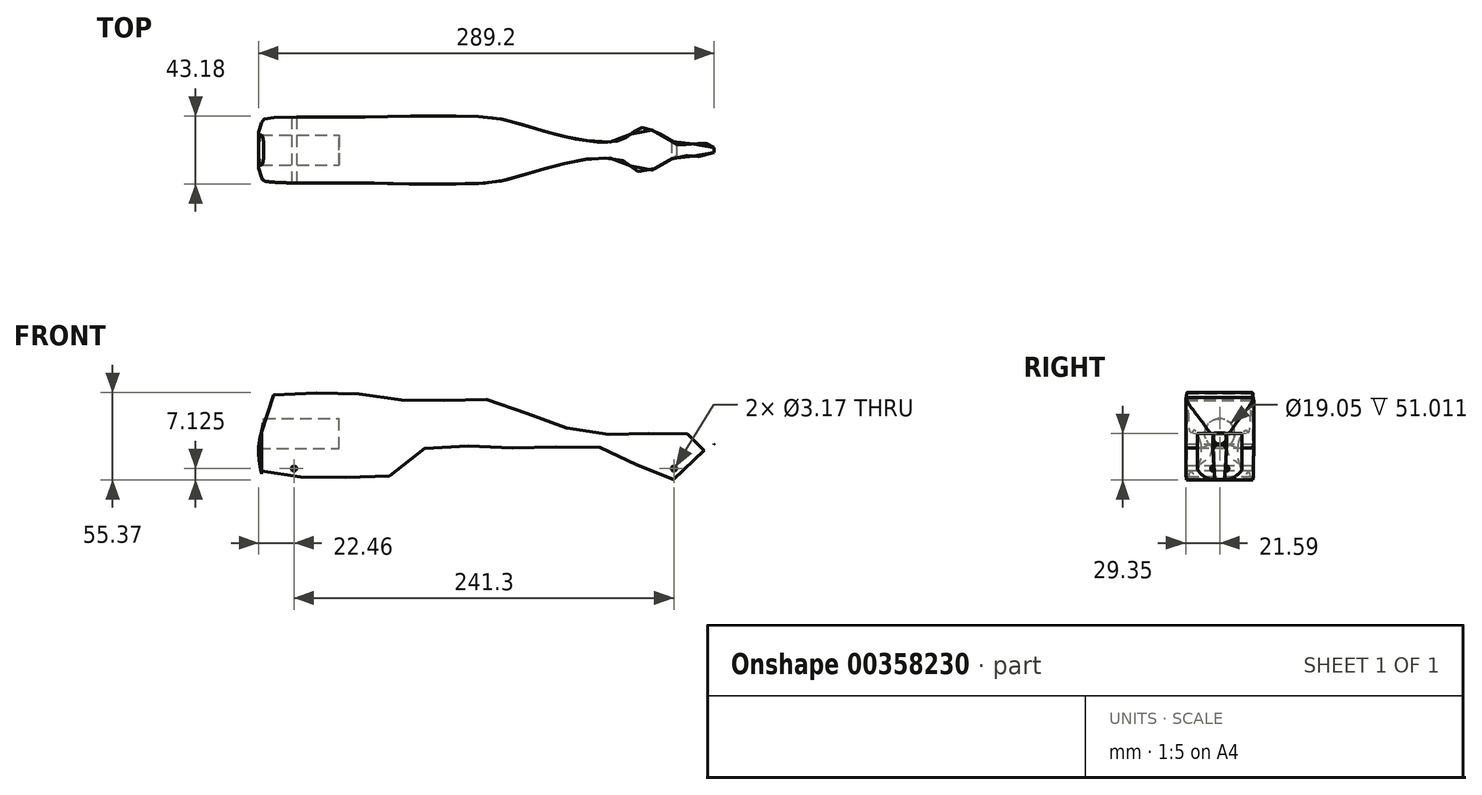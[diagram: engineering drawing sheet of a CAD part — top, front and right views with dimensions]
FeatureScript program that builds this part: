
annotation { "Feature Type Name" : "Feature", "Feature Type Description" : "" }
export const myFeature = defineFeature(function(context is Context, id is Id, definition is map)
    precondition{}
    {
        {
            var Q0;
            Q0=qCreatedBy(makeId("Front.planeOp"),FACE);
            var sketch = newSketch(context, id + "F0", { "sketchPlane" : qUnion([Q0])});
            skLineSegment(sketch, "E0.bottom", {"start": v(-146.05, 31.75) * mm, "end": v(146.05, 31.75) * mm, "construction": true});
            skLineSegment(sketch, "E0.top", {"start": v(-146.05, -31.75) * mm, "end": v(146.05, -31.75) * mm, "construction": true});
            skLineSegment(sketch, "E0.right", {"start": v(146.05, 31.75) * mm, "end": v(146.05, -31.75) * mm, "construction": true});
            skFitSpline(sketch, "E1", {"points": [v(-143.09, -9.52) * mm, v(-140.24, 6.5) * mm, v(-137.4, 21.47) * mm, v(-129.39, 25.57) * mm, v(-119.06, 25.57) * mm, v(-83.25, 25.57) * mm, v(-57.61, 21.5) * mm, v(-39.32, 21.5) * mm, v(-11.8, 21.5) * mm, v(-4.58, 22.81) * mm, v(38.07, 8.64) * mm, v(68.73, 0) * mm, v(103.53, 0) * mm, v(120, 0) * mm, v(127.33, 0) * mm, v(146.05, -6.5) * mm, v(136.49, -12.9) * mm, v(121.94, -28.82) * mm, v(77.89, -10.14) * mm, v(48.58, -8.33) * mm, v(26.63, -9.13) * mm, v(0, -8.6) * mm, v(-18.77, -6.87) * mm, v(-37.56, -9.27) * mm, v(-61.29, -27.5) * mm, v(-82.68, -28.25) * mm, v(-109.82, -27.5) * mm, v(-137.27, -28.02) * mm, v(-139.97, -28.02) * mm, v(-143.09, -9.52) * mm]});
            skLineSegment(sketch, "E2.bottom", {"start": v(-146.05, 9.52) * mm, "end": v(-95.25, 9.52) * mm, "construction": true});
            skLineSegment(sketch, "E2.top", {"start": v(-143.09, -9.52) * mm, "end": v(-95.25, -9.52) * mm, "construction": true});
            skLineSegment(sketch, "E2.right", {"start": v(-95.25, 9.52) * mm, "end": v(-95.25, -9.52) * mm, "construction": true});
            skLineSegment(sketch, "E3", {"start": v(-146.05, 31.75) * mm, "end": v(-146.05, -31.75) * mm, "construction": true});
            skSolve(sketch);
        }
        {
            var Q0;
            Q0=qCreatedBy(makeId("Top.planeOp"),FACE);
            var sketch = newSketch(context, id + "F1", { "sketchPlane" : qUnion([Q0])});
            skLineSegment(sketch, "E4.bottom", {"start": v(-146.05, 22.22) * mm, "end": v(146.05, 22.23) * mm, "construction": true});
            skLineSegment(sketch, "E4.top", {"start": v(-146.05, -22.23) * mm, "end": v(146.05, -22.22) * mm, "construction": true});
            skLineSegment(sketch, "E4.left", {"start": v(-146.05, 22.22) * mm, "end": v(-146.05, -22.23) * mm, "construction": true});
            skLineSegment(sketch, "E4.right", {"start": v(146.05, 22.22) * mm, "end": v(146.05, -22.22) * mm, "construction": true});
            skLineSegment(sketch, "E5", {"start": v(-146.05, 0) * mm, "end": v(146.05, 0) * mm, "construction": true});
            skFitSpline(sketch, "E6", {"points": [v(-146.05, 0) * mm, v(-142.69, 12.22) * mm, v(-141.13, 16.82) * mm, v(-141.46, 18.87) * mm, v(-94.2, 20.86) * mm, v(-46.02, 21.54) * mm, v(-6.88, 21.32) * mm, v(11.24, 19.62) * mm, v(52.25, 8.3) * mm, v(89.1, 7.1) * mm, v(98.78, 13.98) * mm, v(110.12, 10.97) * mm, v(120.68, 4.63) * mm, v(125.8, 3.23) * mm, v(146.05, 0) * mm], "startDerivative": vector(0, 335.54) * mm, "endDerivative": vector(-69.07, -268.47) * mm});
            skFitSpline(sketch, "E7.MirrorCS", {"points": [v(-146.05, 0) * mm, v(-142.69, -12.22) * mm, v(-141.13, -16.82) * mm, v(-141.46, -18.87) * mm, v(-94.2, -20.86) * mm, v(-46.02, -21.54) * mm, v(-6.88, -21.32) * mm, v(11.24, -19.62) * mm, v(52.25, -8.3) * mm, v(89.1, -7.1) * mm, v(98.78, -13.98) * mm, v(110.12, -10.97) * mm, v(120.68, -4.63) * mm, v(125.8, -3.23) * mm, v(146.05, 0) * mm], "startDerivative": vector(0, -335.54) * mm, "endDerivative": vector(-69.07, 268.47) * mm});
            skLineSegment(sketch, "E8.MirrorCS", {"start": v(-146.05, -22.23) * mm, "end": v(146.05, -22.23) * mm});
            skSolve(sketch);
        }
        {
            var Q0;
            Q0=qCreatedBy(makeId("Right.planeOp"),FACE);
            var sketch = newSketch(context, id + "F2", { "sketchPlane" : qUnion([Q0])});
            skCircle(sketch, "E9", {"center": v(0, 0) * mm, "radius": 9.53 * mm});
            skSolve(sketch);
        }
        {
            var Q0;
            Q0=qCreatedBy(makeId("Front.planeOp"),FACE);
            var sketch = newSketch(context, id + "F3", { "sketchPlane" : qUnion([Q0])});
            skCircle(sketch, "E10", {"center": v(-120.65, -22.22) * mm, "radius": 1.59 * mm});
            skCircle(sketch, "E11", {"center": v(120.65, -22.23) * mm, "radius": 1.59 * mm});
            skSolve(sketch);
        }
        {
            var Q0;
            Q0=qSketchRegion(id+"F0",true);
            extrude(context, id + "F4", {"entities" : qUnion([Q0]), "depth" : 44.45 * mm, "symmetric" : true});
        }
        {
            var Q0;
            Q0=qSketchRegion(id+"F1",true);
            extrude(context, id + "F5", {"entities" : qUnion([Q0]), "operationType" : NewBodyOperationType.INTERSECT, "endBound" : BoundingType.THROUGH_ALL, "oppositeDirection" : true, "depth" : 60.96 * mm, "hasSecondDirection" : true, "secondDirectionBound" : BoundingType.THROUGH_ALL, "secondDirectionOppositeDirection" : false, "secondDirectionDepth" : 25.4 * mm});
        }
        {
            var Q0;
            Q0=qSketchRegion(id+"F2",true);
            extrude(context, id + "F6", {"entities" : qUnion([Q0]), "operationType" : NewBodyOperationType.REMOVE, "oppositeDirection" : true, "depth" : 152.4 * mm, "hasSecondDirection" : true, "secondDirectionOppositeDirection" : true, "secondDirectionDepth" : 92.07 * mm});
        }
        {
            var Q0;
            Q0=qSketchRegion(id+"F3",true);
            extrude(context, id + "F7", {"entities" : qUnion([Q0]), "operationType" : NewBodyOperationType.REMOVE, "oppositeDirection" : true, "depth" : 50.8 * mm, "symmetric" : true});
        }
    });
